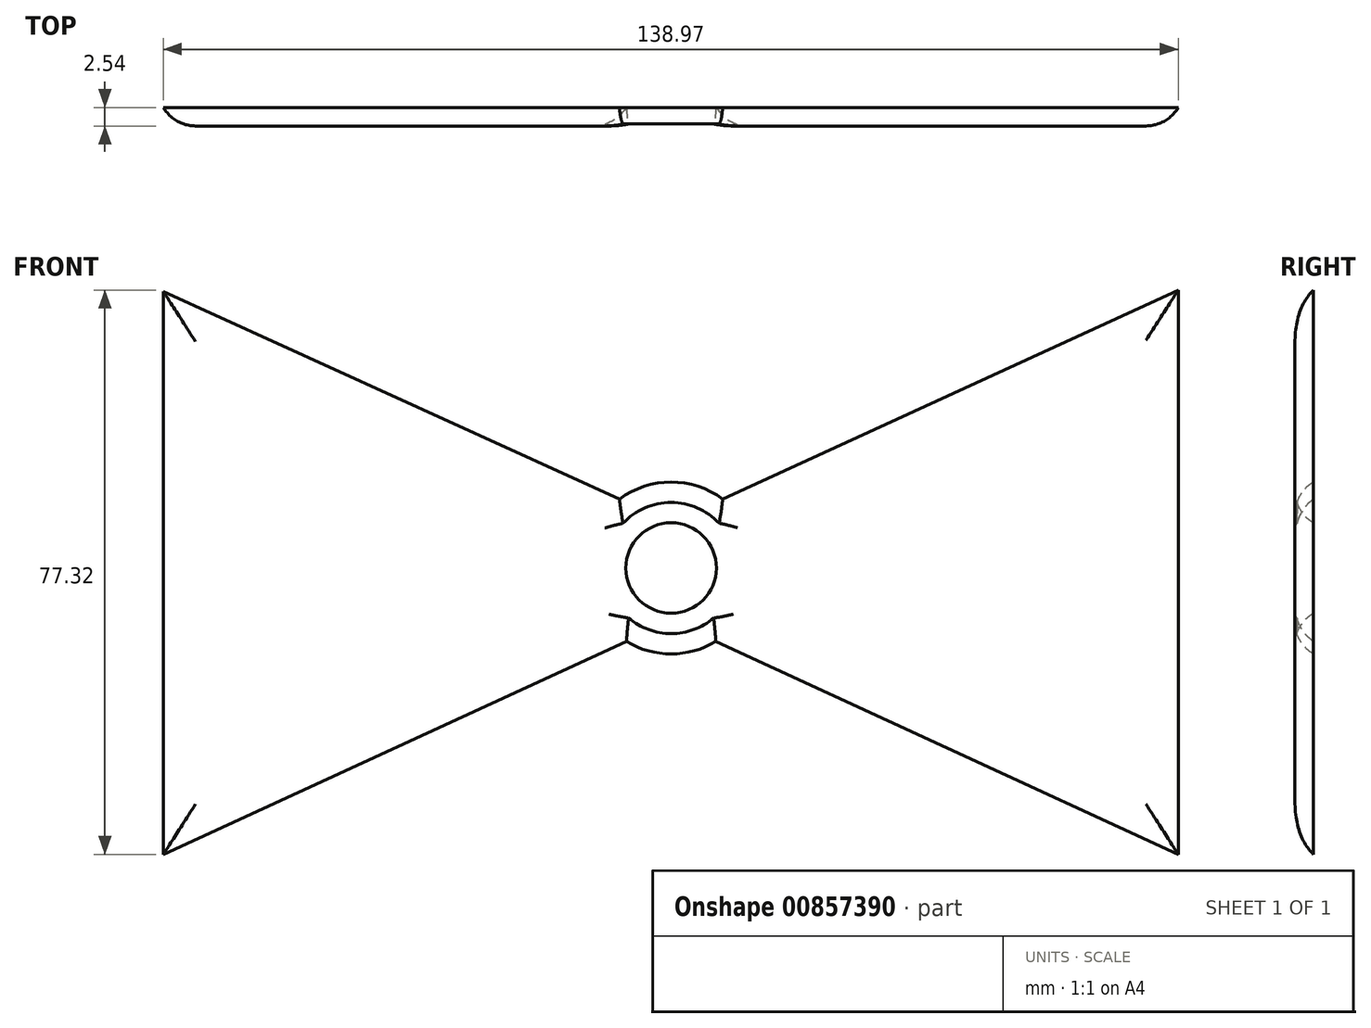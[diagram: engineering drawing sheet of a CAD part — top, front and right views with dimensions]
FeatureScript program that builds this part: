
annotation { "Feature Type Name" : "Feature", "Feature Type Description" : "" }
export const myFeature = defineFeature(function(context is Context, id is Id, definition is map)
    precondition{}
    {
        {
            var Q0;
            Q0=qCreatedBy(makeId("Front.planeOp"),FACE);
            var sketch = newSketch(context, id + "F0", { "sketchPlane" : qUnion([Q0])});
            skLineSegment(sketch, "E0", {"start": v(-93.85, 82.37) * mm, "end": v(-93.85, 5.27) * mm});
            skLineSegment(sketch, "E1", {"start": v(-93.85, 5.27) * mm, "end": v(-24.31, 37.25) * mm});
            skLineSegment(sketch, "E2", {"start": v(-24.31, 37.25) * mm, "end": v(45.12, 5.27) * mm});
            skLineSegment(sketch, "E3", {"start": v(45.12, 5.27) * mm, "end": v(45.12, 82.59) * mm});
            skLineSegment(sketch, "E4", {"start": v(45.12, 82.59) * mm, "end": v(-24.31, 50.7) * mm});
            skLineSegment(sketch, "E5", {"start": v(-24.31, 50.7) * mm, "end": v(-93.85, 82.37) * mm});
            skCircle(sketch, "E6", {"center": v(-24.31, 44.51) * mm, "radius": 11.78 * mm});
            skCircle(sketch, "E7", {"center": v(-24.31, 44.51) * mm, "radius": 6.2 * mm});
            skSolve(sketch);
        }
        {
            var Q0;
            {var subQ0=sQuery(id+"F0.wireOp",EDGE,"E0");Q0=makeQuery(id+"F0.imprint","IMPRINT",FACE,{"disambiguationData":[TD([[makeQuery(id+"F0.imprint","IMPRINT",EDGE,{"derivedFrom":subQ0}),1.0]])]});}
            var Q1;
            {var subQ0=sQuery(id+"F0.wireOp",EDGE,"E2");var subQ1=sQuery(id+"F0.wireOp",EDGE,"E1");var subQ2=makeQuery(id+"F0.imprint","INTERSECT",VERTEX,{"derivedFrom":[subQ1,subQ0]});Q1=makeQuery(id+"F0.imprint","IMPRINT",FACE,{"disambiguationData":[TD([[makeQuery(id+"F0.imprint","IMPRINT",EDGE,{"disambiguationData":[TD([[subQ2,1.0]])],"derivedFrom":subQ1}),-1.0]])]});}
            var Q2;
            {var subQ1=sQuery(id+"F0.wireOp",EDGE,"E4");var subQ3=sQuery(id+"F0.wireOp",EDGE,"E6");var subQ4=makeQuery(id+"F0.imprint","INTERSECT",VERTEX,{"derivedFrom":[subQ1,subQ3]});Q2=makeQuery(id+"F0.imprint","IMPRINT",FACE,{"disambiguationData":[TD([[makeQuery(id+"F0.imprint","IMPRINT",EDGE,{"disambiguationData":[TD([[subQ4,-1.0]])],"derivedFrom":subQ3}),1.0]])]});}
            var Q3;
            {var subQ0=sQuery(id+"F0.wireOp",EDGE,"E7");Q3=makeQuery(id+"F0.imprint","IMPRINT",FACE,{"disambiguationData":[TD([[makeQuery(id+"F0.imprint","IMPRINT",EDGE,{"derivedFrom":subQ0}),-1.0]])]});}
            var Q4;
            {var subQ0=sQuery(id+"F0.wireOp",EDGE,"E3");Q4=makeQuery(id+"F0.imprint","IMPRINT",FACE,{"disambiguationData":[TD([[makeQuery(id+"F0.imprint","IMPRINT",EDGE,{"derivedFrom":subQ0}),1.0]])]});}
            extrude(context, id + "F1", {"entities" : qUnion([Q0, Q1, Q2, Q3, Q4]), "depth" : 2.54 * mm, "offsetDistance" : 25.4 * mm});
        }
        {
            var Q0;
            Q0=makeQuery(id+"F1.opExtrude","CAP_EDGE",EDGE,{"disambiguationData":[OSD([sQuery(id+"F0.wireOp",EDGE,"E0")])],"isStart":false});
            var Q1;
            Q1=makeQuery(id+"F1.opExtrude","CAP_EDGE",EDGE,{"disambiguationData":[OSD([sQuery(id+"F0.wireOp",EDGE,"E5")])],"isStart":false});
            var Q2;
            Q2=makeQuery(id+"F1.opExtrude","CAP_EDGE",EDGE,{"disambiguationData":[OSD([sQuery(id+"F0.wireOp",EDGE,"E1")])],"isStart":false});
            var Q3;
            {var subQ0=sQuery(id+"F0.wireOp",EDGE,"E6");Q3=makeQuery(id+"F1.opExtrude","CAP_EDGE",EDGE,{"disambiguationData":[OSD([subQ0]),TDD([makeQuery(id+"F0.imprint","IMPRINT",EDGE,{"disambiguationData":[TD([[makeQuery(id+"F0.imprint","INTERSECT",VERTEX,{"derivedFrom":[sQuery(id+"F0.wireOp",EDGE,"E1"),subQ0]}),-1.0]])],"derivedFrom":subQ0})])],"isStart":false});}
            var Q4;
            {var subQ0=sQuery(id+"F0.wireOp",EDGE,"E6");Q4=makeQuery(id+"F1.opExtrude","CAP_EDGE",EDGE,{"disambiguationData":[OSD([subQ0]),TDD([makeQuery(id+"F0.imprint","IMPRINT",EDGE,{"disambiguationData":[TD([[makeQuery(id+"F0.imprint","INTERSECT",VERTEX,{"derivedFrom":[sQuery(id+"F0.wireOp",EDGE,"E4"),subQ0]}),-1.0]])],"derivedFrom":subQ0})])],"isStart":false});}
            var Q5;
            Q5=makeQuery(id+"F1.opExtrude","CAP_EDGE",EDGE,{"disambiguationData":[OSD([sQuery(id+"F0.wireOp",EDGE,"E4")])],"isStart":false});
            var Q6;
            Q6=makeQuery(id+"F1.opExtrude","CAP_EDGE",EDGE,{"disambiguationData":[OSD([sQuery(id+"F0.wireOp",EDGE,"E3")])],"isStart":false});
            var Q7;
            Q7=makeQuery(id+"F1.opExtrude","CAP_EDGE",EDGE,{"disambiguationData":[OSD([sQuery(id+"F0.wireOp",EDGE,"E2")])],"isStart":false});
            var Q8;
            Q8=makeQuery(id+"F1.opExtrude","CAP_EDGE",EDGE,{"disambiguationData":[OSD([sQuery(id+"F0.wireOp",EDGE,"E7")])],"isStart":false});
            fillet(context, id + "F2", {"entities" : qUnion([Q0, Q1, Q2, Q3, Q4, Q5, Q6, Q7, Q8]), "radius" : 5.08 * mm, "tangentPropagation" : true, "allowEdgeOverflow" : false});
        }
    });
